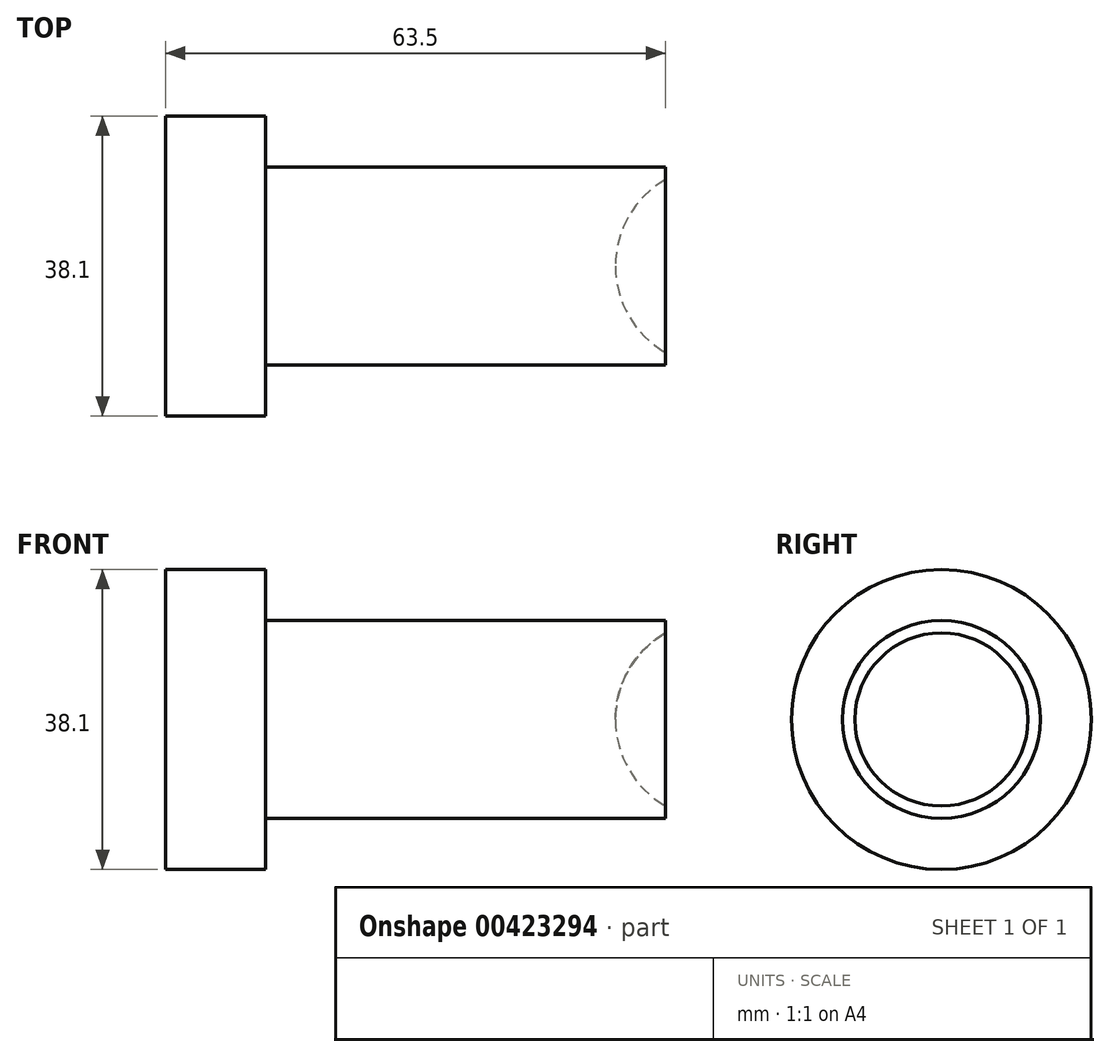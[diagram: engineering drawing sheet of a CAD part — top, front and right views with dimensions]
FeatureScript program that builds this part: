
annotation { "Feature Type Name" : "Feature", "Feature Type Description" : "" }
export const myFeature = defineFeature(function(context is Context, id is Id, definition is map)
    precondition{}
    {
        {
            var Q0;
            Q0=qCreatedBy(makeId("Front.planeOp"),FACE);
            var sketch = newSketch(context, id + "F0", { "sketchPlane" : qUnion([Q0])});
            skLineSegment(sketch, "E0.bottom", {"start": v(0, 0) * mm, "end": v(-12.7, 0) * mm});
            skLineSegment(sketch, "E0.top", {"start": v(0, 19.05) * mm, "end": v(-12.7, 19.05) * mm});
            skLineSegment(sketch, "E0.left", {"start": v(0, 0) * mm, "end": v(0, 19.05) * mm});
            skLineSegment(sketch, "E0.right", {"start": v(-12.7, 0) * mm, "end": v(-12.7, 19.05) * mm});
            skLineSegment(sketch, "E1.bottom", {"start": v(0, 0) * mm, "end": v(50.8, 0) * mm});
            skLineSegment(sketch, "E1.top", {"start": v(0, 12.57) * mm, "end": v(50.8, 12.57) * mm});
            skLineSegment(sketch, "E1.left", {"start": v(0, 0) * mm, "end": v(0, 12.57) * mm});
            skLineSegment(sketch, "E1.right", {"start": v(50.8, 0) * mm, "end": v(50.8, 12.57) * mm});
            skSolve(sketch);
        }
        {
            var Q0;
            Q0=makeQuery(id+"F0.imprint","IMPRINT",FACE,{"disambiguationData":[TD([[makeQuery(id+"F0.imprint","IMPRINT",EDGE,{"derivedFrom":sQuery(id+"F0.wireOp",EDGE,"E1.bottom")}),1.0]])]});
            var Q1;
            Q1=makeQuery(id+"F0.imprint","IMPRINT",FACE,{"disambiguationData":[TD([[makeQuery(id+"F0.imprint","IMPRINT",EDGE,{"derivedFrom":sQuery(id+"F0.wireOp",EDGE,"E0.bottom")}),-1.0]])]});
            var Q2;
            Q2=sQuery(id+"F0.wireOp",EDGE,"E1.bottom");
            revolve(context, id + "F1", {"entities" : qUnion([Q0, Q1]), "axis" : qUnion([Q2]), "revolveType" : RevolveType.FULL});
        }
        {
            var Q0;
            Q0=qCreatedBy(makeId("Front.planeOp"),FACE);
            var sketch = newSketch(context, id + "F2", { "sketchPlane" : qUnion([Q0])});
            skLineSegment(sketch, "E2.0", {"start": v(50.8, -11) * mm, "end": v(50.8, 11) * mm});
            skArc(sketch, "E3", {"start": v(50.8, 11) * mm, "mid": v(46.15, 6.35) * mm, "end": v(44.45, 0) * mm});
            skLineSegment(sketch, "E4", {"start": v(50.8, 11) * mm, "end": v(50.8, 0) * mm});
            skLineSegment(sketch, "E5", {"start": v(44.45, 0) * mm, "end": v(50.8, 0) * mm});
            skPoint(sketch, "E6.orphan", {"position": v(50.8, 12.57) * mm});
            skPoint(sketch, "E7.orphan", {"position": v(50.8, -12.57) * mm});
            skSolve(sketch);
        }
        {
            var Q0;
            Q0 = qSketchRegion(id + "F2", true);
            var Q1;
            Q1=sQuery(id+"F2.wireOp",EDGE,"E5");
            revolve(context, id + "F3", {"operationType" : NewBodyOperationType.REMOVE, "entities" : qUnion([Q0]), "axis" : qUnion([Q1]), "revolveType" : RevolveType.FULL, "oppositeDirection" : true});
        }
    });
